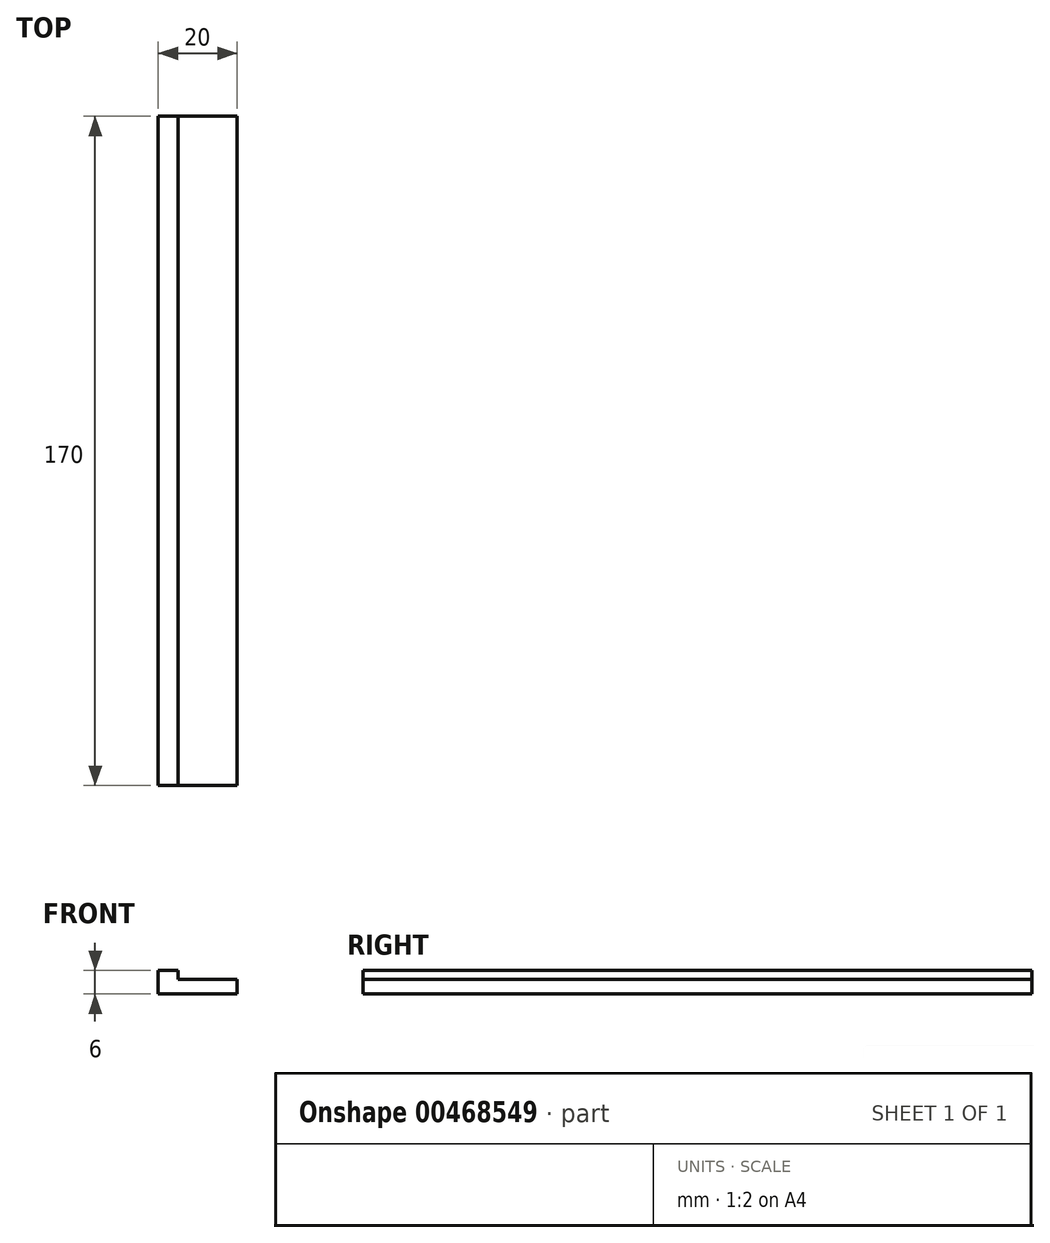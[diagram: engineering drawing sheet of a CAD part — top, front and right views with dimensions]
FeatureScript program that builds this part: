
annotation { "Feature Type Name" : "Feature", "Feature Type Description" : "" }
export const myFeature = defineFeature(function(context is Context, id is Id, definition is map)
    precondition{}
    {
        {
            var Q0;
            Q0=qCreatedBy(makeId("Top.planeOp"),FACE);
            var sketch = newSketch(context, id + "F0", { "sketchPlane" : qUnion([Q0])});
            skLineSegment(sketch, "E0.bottom", {"start": v(0, 100.84) * mm, "end": v(20, 100.84) * mm});
            skLineSegment(sketch, "E0.top", {"start": v(0, -69.16) * mm, "end": v(20, -69.16) * mm});
            skLineSegment(sketch, "E0.left", {"start": v(0, 100.84) * mm, "end": v(0, -69.16) * mm});
            skLineSegment(sketch, "E0.right", {"start": v(20, 100.84) * mm, "end": v(20, -69.16) * mm});
            skSolve(sketch);
        }
        {
            var Q0;
            Q0 = qSketchRegion(id + "F0", true);
            extrude(context, id + "F1", {"entities" : qUnion([Q0]), "depth" : 3.7 * mm, "offsetDistance" : 25 * mm});
        }
        {
            var Q0;
            Q0=makeQuery(id+"F1.opExtrude","CAP_FACE",FACE,{"disambiguationData":[OSD([sQuery(id+"F0.wireOp",EDGE,"E0.bottom"),sQuery(id+"F0.wireOp",EDGE,"E0.top"),sQuery(id+"F0.wireOp",EDGE,"E0.left"),sQuery(id+"F0.wireOp",EDGE,"E0.right")])],"isStart":false});
            var sketch = newSketch(context, id + "F2", { "sketchPlane" : qUnion([Q0])});
            skLineSegment(sketch, "E1.bottom", {"start": v(0, 100.84) * mm, "end": v(5, 100.84) * mm});
            skLineSegment(sketch, "E1.top", {"start": v(0, -69.16) * mm, "end": v(5, -69.16) * mm});
            skLineSegment(sketch, "E1.left", {"start": v(0, 100.84) * mm, "end": v(0, -69.16) * mm});
            skLineSegment(sketch, "E1.right", {"start": v(5, 100.84) * mm, "end": v(5, -69.16) * mm});
            skSolve(sketch);
        }
        {
            var Q0;
            Q0 = qSketchRegion(id + "F2", true);
            extrude(context, id + "F3", {"entities" : qUnion([Q0]), "operationType" : NewBodyOperationType.ADD, "depth" : 2.3 * mm, "offsetDistance" : 25 * mm});
        }
    });
